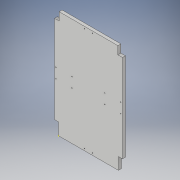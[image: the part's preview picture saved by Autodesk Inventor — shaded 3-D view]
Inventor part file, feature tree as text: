
AUTODESK INVENTOR PART (.ipt)
format: ipt  version: 2018 (Build 220112000, 112)  size: 155,136 bytes
history: native  units: in
note: dims shown in document units (in); Inventor stores cm internally (conversion verified against a paired STEP export)
features: sketch x3, extrude x2
ambient origin geometry x8: Origin, YZ Plane, XZ Plane, XY Plane, X Axis, Y Axis, Z Axis, Center Point
bodies: Solid1 (feature_tree)
feature tree (5):
  extrude  "Extrusion1"  Depth=1.0in
  sketch  "Sketch2"  dims[d2=22.0in d3=1.125in]
  extrude  "Extrusion2"  Depth=1.125in
  sketch  "Sketch1"  dims[d0=3.0in d1=1.0in]
  sketch  "Sketch3"  dims[d4=2.0in d5=14.75in d6=1.125in d7=1.0in d8=0.75in d9=0.0in d10=10.47in d11=0.3333in d12=0.0in d13=4.0in d14=9.06in d15=0.2031in d16=1.0in d17=0.5in d19=0.2031in d20=1.0in d21=0.5in d22=1.0in d23=0.0in d25=11.9402in d26=0.4443in d27=4.0in d28=2.47in d29=0.2031in]
